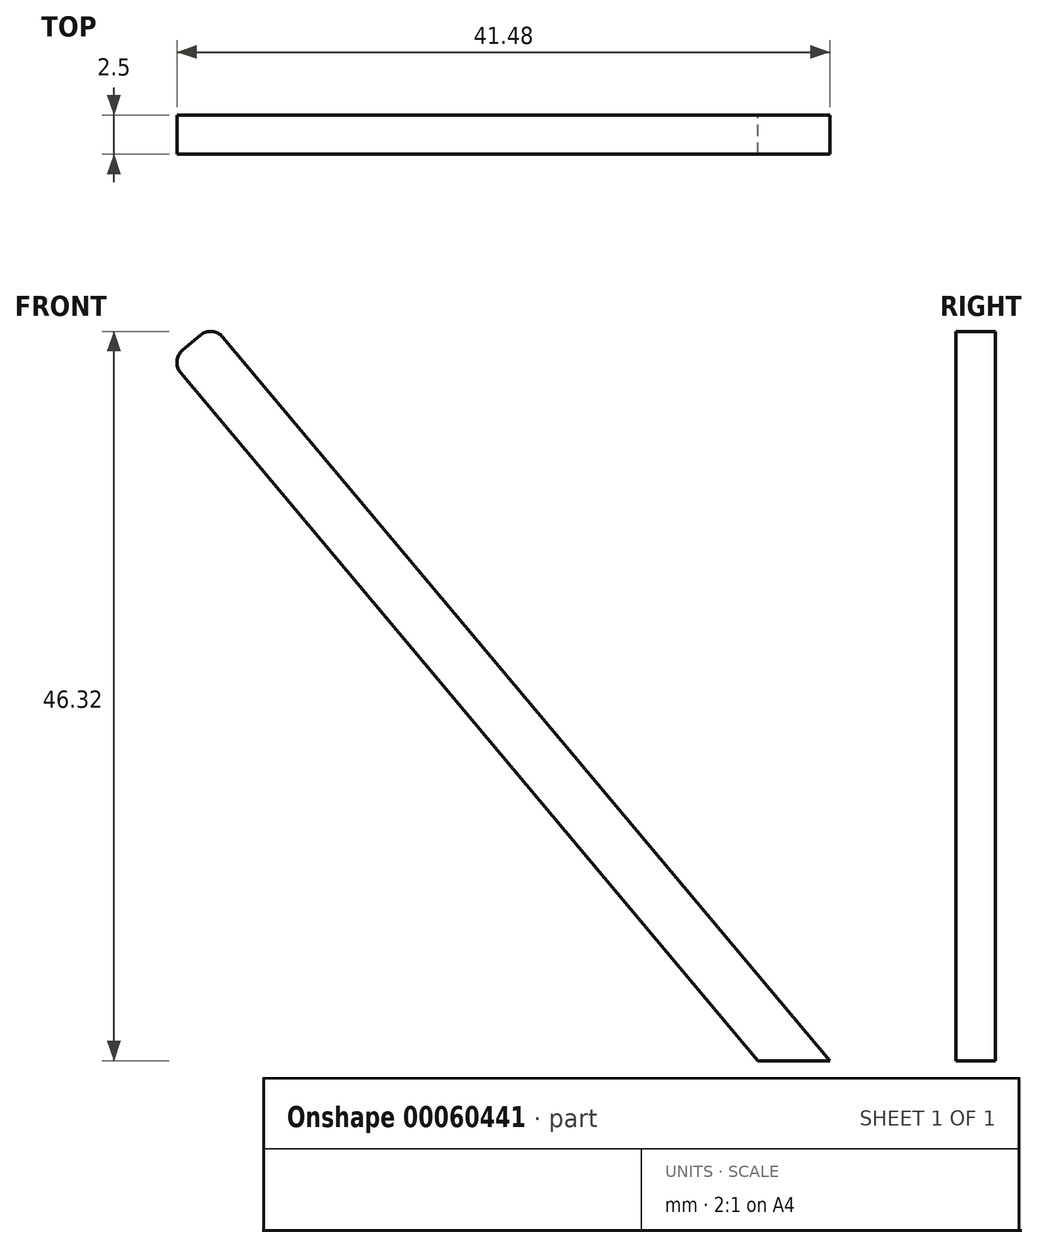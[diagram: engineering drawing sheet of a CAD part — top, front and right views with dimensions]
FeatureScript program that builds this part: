
annotation { "Feature Type Name" : "Feature", "Feature Type Description" : "" }
export const myFeature = defineFeature(function(context is Context, id is Id, definition is map)
    precondition{}
    {
        {
            var Q0;
            Q0=qCreatedBy(makeId("Front.planeOp"),FACE);
            var sketch = newSketch(context, id + "F0", { "sketchPlane" : qUnion([Q0])});
            skLineSegment(sketch, "E0.bottom", {"start": v(0, 0) * mm, "end": v(-3.5, 0) * mm});
            skLineSegment(sketch, "E0.top", {"start": v(0, 61) * mm, "end": v(-3.5, 61) * mm});
            skLineSegment(sketch, "E0.left", {"start": v(0, 0) * mm, "end": v(0, 61) * mm});
            skLineSegment(sketch, "E0.right", {"start": v(-3.5, 0) * mm, "end": v(-3.5, 61) * mm});
            skPoint(sketch, "E1", {"position": v(-1.75, 30.5) * mm});
            skSolve(sketch);
        }
        {
            var Q0;
            Q0 = qSketchRegion(id + "F0", true);
            extrude(context, id + "F1", {"entities" : qUnion([Q0]), "depth" : 2.5 * mm});
        }
        {
            var Q0;
            Q0=makeQuery(id+"F1.opExtrude","SWEPT_EDGE",EDGE,{"disambiguationData":[OSD([sQuery(id+"F0.wireOp",EDGE,"E0.top"),sQuery(id+"F0.wireOp",EDGE,"E0.right")])]});
            var Q1;
            Q1=makeQuery(id+"F1.opExtrude","SWEPT_EDGE",EDGE,{"disambiguationData":[OSD([sQuery(id+"F0.wireOp",EDGE,"E0.top"),sQuery(id+"F0.wireOp",EDGE,"E0.left")])]});
            fillet(context, id + "F2", {"entities" : qUnion([Q0, Q1]), "radius" : 1 * mm, "allowEdgeOverflow" : false});
        }
        {
            var Q0;
            Q0=makeQuery(id+"F1.opExtrude","SWEPT_BODY",BODY,{"disambiguationData":[OSD([sQuery(id+"F0.wireOp",EDGE,"E0.bottom"),sQuery(id+"F0.wireOp",EDGE,"E0.top"),sQuery(id+"F0.wireOp",EDGE,"E0.left"),sQuery(id+"F0.wireOp",EDGE,"E0.right")])]});
            var Q1;
            Q1=makeQuery(id+"F1.opExtrude","SWEPT_EDGE",EDGE,{"disambiguationData":[OSD([sQuery(id+"F0.wireOp",EDGE,"E0.bottom"),sQuery(id+"F0.wireOp",EDGE,"E0.left")])]});
            transform(context, id + "F3", {"entities" : qUnion([Q0]), "transformType" : TransformType.ROTATION, "transformAxis" : qUnion([Q1]), "angle" : 40 * degree, "oppositeDirection" : true, "makeCopy" : false});
        }
        {
            var Q0;
            Q0=qCreatedBy(makeId("Front.planeOp"),FACE);
            var sketch = newSketch(context, id + "F4", { "sketchPlane" : qUnion([Q0])});
            skLineSegment(sketch, "E2.bottom", {"start": v(-42.82, 0) * mm, "end": v(16.65, 0) * mm});
            skLineSegment(sketch, "E2.top", {"start": v(-42.82, -9.75) * mm, "end": v(16.65, -9.75) * mm});
            skLineSegment(sketch, "E2.left", {"start": v(-42.82, 0) * mm, "end": v(-42.82, -9.75) * mm});
            skLineSegment(sketch, "E2.right", {"start": v(16.65, 0) * mm, "end": v(16.65, -9.75) * mm});
            skSolve(sketch);
        }
        {
            var Q0;
            Q0 = qSketchRegion(id + "F4", true);
            extrude(context, id + "F5", {"entities" : qUnion([Q0]), "depth" : 25 * mm});
        }
        {
            var Q0;
            Q0=makeQuery(id+"F5.opExtrude","SWEPT_BODY",BODY,{"disambiguationData":[OSD([sQuery(id+"F4.wireOp",EDGE,"E2.bottom"),sQuery(id+"F4.wireOp",EDGE,"E2.top"),sQuery(id+"F4.wireOp",EDGE,"E2.left"),sQuery(id+"F4.wireOp",EDGE,"E2.right")])]});
            var Q1;
            Q1=makeQuery(id+"F1.opExtrude","SWEPT_BODY",BODY,{"disambiguationData":[OSD([sQuery(id+"F0.wireOp",EDGE,"E0.bottom"),sQuery(id+"F0.wireOp",EDGE,"E0.top"),sQuery(id+"F0.wireOp",EDGE,"E0.left"),sQuery(id+"F0.wireOp",EDGE,"E0.right")])]});
            booleanBodies(context, id + "F6", {"operationType" : BooleanOperationType.SUBTRACTION, "tools" : qUnion([Q0]), "targets" : qUnion([Q1])});
        }
    });
